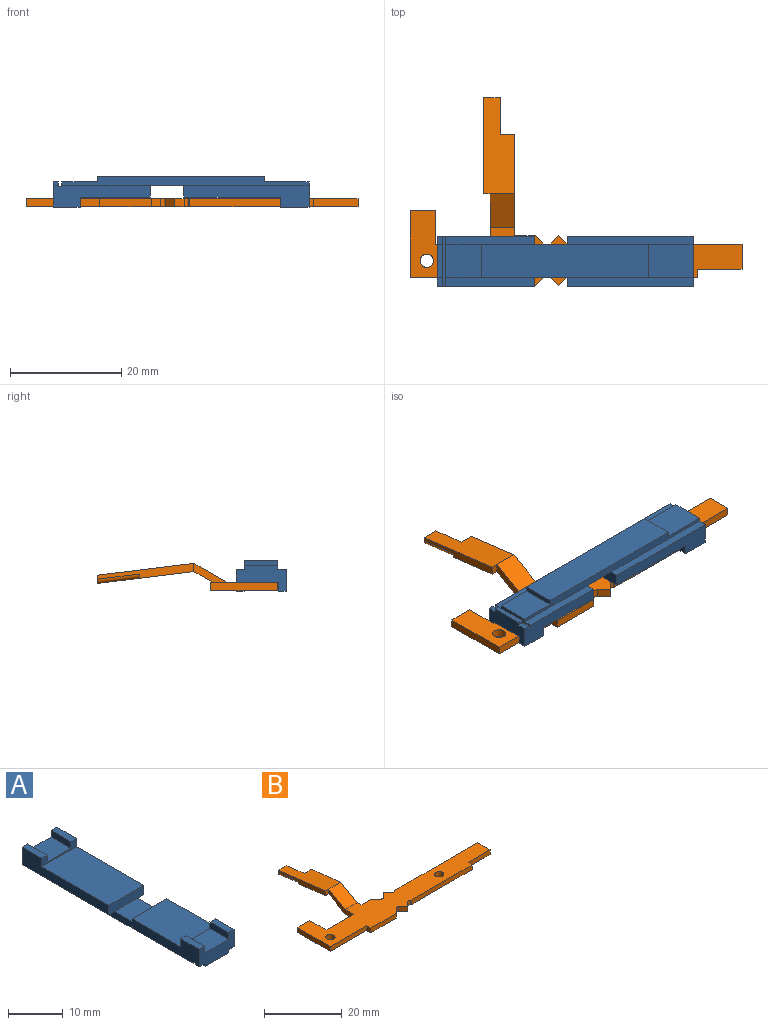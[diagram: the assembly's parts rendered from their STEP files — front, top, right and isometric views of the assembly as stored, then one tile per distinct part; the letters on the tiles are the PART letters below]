
ASSEMBLY  parts=2 mates=1
PART A: 42 faces, bbox 9x45.9x5.4 mm
  f0: plane 6x0.9mm, normal (0,0,-1), area 5.4mm2, adj f11,f13,f17,f40
  f1: plane 44.4x1.5mm, normal (-1,0,0), area 53.6mm2, adj f3,f9,f10,f12,f14,f15,f16,f18
  f2: plane 44.4x1.5mm, normal (1,0,0), area 53.6mm2, adj f5,f9,f10,f12,f14,f15,f16,f18
  f3: plane 15.9x1.5mm, normal (0,0,-1), area 23.9mm2, adj f1,f4,f27,f39
  f4: plane 17.4x3.9mm, normal (-1,0,0), area 45mm2, adj f3,f8,f17,f25,f27,f30,f36,f39
  f5: plane 15.9x1.5mm, normal (0,0,-1), area 23.8mm2, adj f2,f26,f27,f39
  f6: plane 6.15x4.8mm, normal (0,0,1), area 29.5mm2, adj f17,f30,f35,f37
  f7: plane 6.15x5.1mm, normal (0,0,1), area 31.4mm2, adj f16,f29,f31,f33
  f8: plane 12.6x9mm, normal (0,0,1), area 113.4mm2, adj f4,f26,f27,f30
  f9: plane 6x6mm, normal (0,0,1), area 36mm2, adj f1,f2,f22,f27
  f10: plane 6x0.9mm, normal (0,1,0), area 5.4mm2, adj f1,f2,f14,f18
  f11: plane 0.9x0.6mm, normal (-1,0,0), area 0.5mm2, adj f0,f17,f25,f40
  f12: plane 6x0.9mm, normal (0,-1,0), area 5.4mm2, adj f1,f2,f14,f15
  f13: plane 0.9x0.6mm, normal (1,0,0), area 0.5mm2, adj f0,f17,f28,f40
  f14: plane 30x6mm, normal (0,0,-1), area 180mm2, adj f1,f2,f10,f12
  f15: plane 6.45x6mm, normal (0,0,-1), area 38.7mm2, adj f1,f2,f12,f39
  f16: plane 9x4.5mm, normal (0,1,0), area 29.5mm2, adj f1,f2,f7,f18,f19,f20,f21,f24
  f17: plane 9x4.5mm, normal (0,-1,0), area 29.5mm2, adj f0,f4,f6,f11,f13,f25,f26,f28
  f18: plane 7.95x6mm, normal (0,0,-1), area 47.7mm2, adj f1,f2,f10,f16
  f19: plane 22.5x1.5mm, normal (0,0,-1), area 33.7mm2, adj f1,f16,f21,f22
  f20: plane 22.5x3.9mm, normal (1,0,0), area 56.4mm2, adj f16,f22,f23,f24,f29,f34
  f21: plane 22.5x3.9mm, normal (-1,0,0), area 56.4mm2, adj f16,f19,f22,f23,f29,f32
  f22: plane 9x2.1mm, normal (0,-1,0), area 18.9mm2, adj f9,f19,f20,f21,f23,f24
  f23: plane 17.4x9mm, normal (0,0,1), area 156.6mm2, adj f20,f21,f22,f29
  f24: plane 22.5x1.5mm, normal (0,0,-1), area 33.7mm2, adj f2,f16,f20,f22
  f25: plane 1.5x0.9mm, normal (0,0,-1), area 1.4mm2, adj f4,f11,f17,f40
  f26: plane 17.4x3.9mm, normal (1,0,0), area 45mm2, adj f5,f8,f17,f27,f28,f30,f38,f39
  f27: plane 9x2.1mm, normal (0,1,0), area 18.9mm2, adj f3,f4,f5,f8,f9,f26
  f28: plane 1.5x0.9mm, normal (0,0,-1), area 1.4mm2, adj f13,f17,f26,f40
  f29: plane 9x1.8mm, normal (0,-1,0), area 7mm2, adj f7,f20,f21,f23,f31,f32,f33,f34
  f30: plane 9x1.8mm, normal (0,1,0), area 7mm2, adj f4,f6,f8,f26,f35,f36,f37,f38
  f31: plane 5.1x1.5mm, normal (1,0,0), area 7.7mm2, adj f7,f16,f29,f32
  f32: plane 5.1x1.43mm, normal (0,0,1), area 7.3mm2, adj f16,f21,f29,f31
  f33: plane 5.1x1.5mm, normal (-1,0,0), area 7.7mm2, adj f7,f16,f29,f34
  f34: plane 5.1x1.43mm, normal (0,0,1), area 7.3mm2, adj f16,f20,f29,f33
  f35: plane 4.8x1.5mm, normal (1,0,0), area 7.2mm2, adj f6,f17,f30,f36
  f36: plane 4.8x1.43mm, normal (0,0,1), area 6.8mm2, adj f4,f17,f30,f35
  f37: plane 4.8x1.5mm, normal (-1,0,0), area 7.2mm2, adj f6,f17,f30,f38
  f38: plane 4.8x1.43mm, normal (0,0,1), area 6.8mm2, adj f17,f26,f30,f37
  f39: plane 9x0.9mm, normal (0,-1,0), area 6.3mm2, adj f1,f2,f3,f4,f5,f15,f26,f41
  f40: plane 9x0.9mm, normal (0,1,0), area 6.3mm2, adj f0,f4,f11,f13,f25,f26,f28,f41
  f41: plane 9x0.6mm, normal (0,0,-1), area 5.4mm2, adj f4,f26,f39,f40
PART B: 42 faces, bbox 59.6x33.9x4.9 mm
  f0: plane 12x1.47mm, normal (-1,0,0), area 17.6mm2, adj f1,f27,f29,f30
  f1: plane 13.2x1.47mm, normal (0,-1,0), area 19.4mm2, adj f0,f2,f29,f30
  f2: plane 1.5x1.47mm, normal (-1,0,0), area 2.2mm2, adj f1,f3,f29,f30
  f3: plane 9.3x1.47mm, normal (0,-1,0), area 13.7mm2, adj f2,f4,f29,f30
  f4: plane 1.68x1.68mm, normal (0.71,-0.71,0), area 3.5mm2, adj f3,f5,f29,f30
  f5: cylinder r=0.6mm len=1.47mm, axis (0,0,-1), area 1.4mm2, adj f4,f6,f29,f30
  f6: plane 1.68x1.68mm, normal (-0.71,-0.71,0), area 3.5mm2, adj f5,f7,f29,f30
  f7: plane 1.68x1.68mm, normal (0.71,-0.71,0), area 3.5mm2, adj f6,f8,f29,f30
  f8: cylinder r=0.6mm len=1.47mm, axis (0,0,-1), area 1.4mm2, adj f7,f9,f29,f30
  f9: plane 1.47x0.18mm, normal (-0.71,-0.71,0), area 0.4mm2, adj f8,f10,f29,f30
  f10: plane 22.2x1.47mm, normal (0,-1,0), area 32.6mm2, adj f9,f11,f29,f30
  f11: plane 1.5x1.47mm, normal (1,0,0), area 2.2mm2, adj f10,f12,f29,f30
  f12: plane 8x1.47mm, normal (0,-1,0), area 11.8mm2, adj f11,f13,f29,f30
  f13: plane 4.5x1.47mm, normal (1,0,0), area 6.6mm2, adj f12,f14,f29,f30
  f14: plane 30.2x1.47mm, normal (0,1,0), area 44.4mm2, adj f13,f15,f29,f30
  f15: plane 1.47x0.18mm, normal (-0.71,0.71,0), area 0.4mm2, adj f14,f16,f29,f30
  f16: cylinder r=0.6mm len=1.47mm, axis (0,0,-1), area 1.4mm2, adj f15,f17,f29,f30
  f17: plane 1.68x1.68mm, normal (0.71,0.71,0), area 3.5mm2, adj f16,f18,f29,f30
  f18: plane 1.68x1.68mm, normal (-0.71,0.71,0), area 3.5mm2, adj f17,f19,f29,f30
  f19: cylinder r=0.6mm len=1.47mm, axis (0,0,-1), area 1.4mm2, adj f18,f20,f29,f30
  f20: plane 1.68x1.68mm, normal (0.71,0.71,0), area 3.5mm2, adj f19,f21,f29,f30
  f21: plane 3.75x1.47mm, normal (0,1,0), area 5.5mm2, adj f20,f22,f29,f30
  f22: plane 18.22x4.93mm, normal (1,0,0), area 26.8mm2, adj f21,f29,f30,f31,f32,f35,f36,f40
  f23: plane 9x4.93mm, normal (-1,0,0), area 13.2mm2, adj f24,f29,f30,f31,f32,f33
  f24: plane 9.9x1.47mm, normal (0,1,0), area 14.6mm2, adj f23,f25,f29,f30
  f25: plane 6x1.47mm, normal (1,0,0), area 8.8mm2, adj f24,f27,f29,f30
  f26: cylinder r=1.2mm len=2.4mm, axis (0,0,-1), area 11.1mm2, adj f29,f30
  f27: plane 4.5x1.47mm, normal (0,1,0), area 6.6mm2, adj f0,f25,f29,f30
  f28: cylinder r=1.2mm len=2.4mm, axis (0,0,-1), area 11.1mm2, adj f29,f30
  f29: plane 59.6x13.5mm, normal (0,0,1), area 401.8mm2, adj f0,f1,f2,f3,f4,f5,f6,f7
  f30: plane 59.6x13.5mm, normal (0,0,-1), area 401.8mm2, adj f0,f1,f2,f3,f4,f5,f6,f7
  f31: plane 6x4.35mm, normal (0,0.5,-0.87), area 30.1mm2, adj f22,f23,f30,f36
  f32: plane 6x4.35mm, normal (0,-0.5,0.87), area 30.1mm2, adj f22,f23,f29,f35
  f33: plane 1.47x1.2mm, normal (0,-1,0), area 1.8mm2, adj f23,f35,f36,f37
  f34: plane 0.76x0.75mm, normal (0,1,0), area 0.1mm2, adj f36,f37,f41
  f35: plane 17.27x5.55mm, normal (0,0.12,0.99), area 79.7mm2, adj f22,f32,f33,f37,f38,f39,f40
  f36: plane 17.27x5.55mm, normal (0,-0.12,-0.99), area 74.1mm2, adj f22,f31,f33,f34,f37,f38,f39,f40
  f37: plane 17.27x2.84mm, normal (-1,0,0), area 19.8mm2, adj f33,f34,f35,f36,f38,f41
  f38: plane 3x1.47mm, normal (0,1,0), area 4.3mm2, adj f35,f36,f37,f39,f41
  f39: plane 6.55x2.27mm, normal (1,0,0), area 9.6mm2, adj f35,f36,f38,f40
  f40: plane 2.55x1.47mm, normal (0,1,0), area 3.7mm2, adj f22,f35,f36,f39
  f41: cylinder r=0.75mm len=7.63mm, axis (0,0.99,-0.12), area 8.8mm2, adj f34,f36,f37,f38
PLACE A rot(axis=(-0.71,-0.71,0),180deg) t=(27.45,-0.73,4.81)mm
PLACE B t=(-0.41,-0.65,0.18)mm
MATE slider A.f17 <-> B.f25  axis (-1,0,0) through (4.5,2.35,0.91)mm
